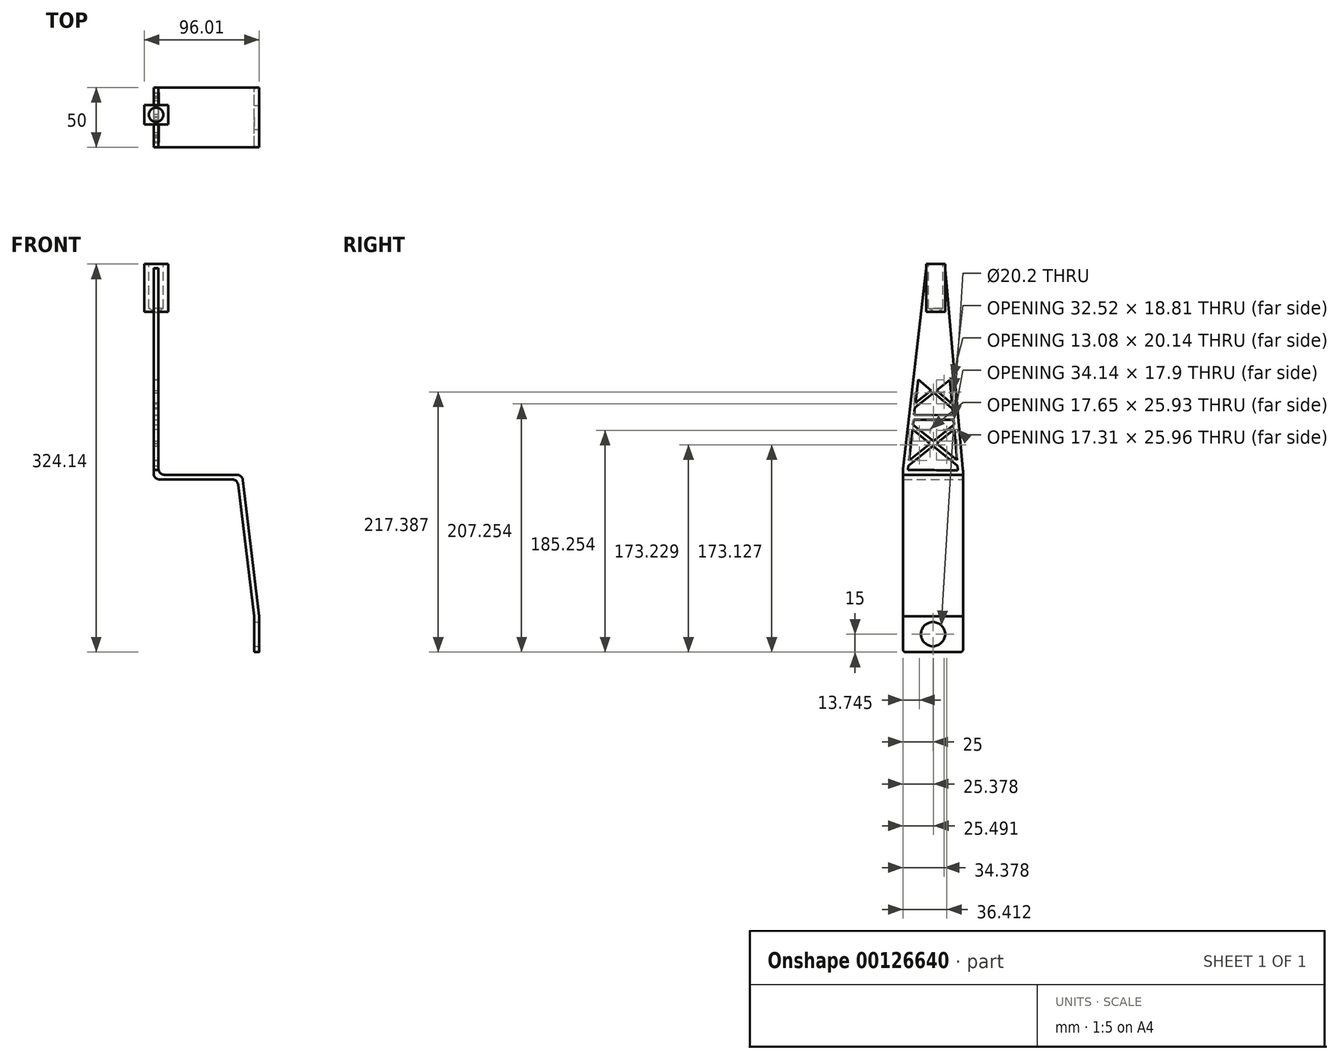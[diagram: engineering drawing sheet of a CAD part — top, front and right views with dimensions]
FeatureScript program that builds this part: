
annotation { "Feature Type Name" : "Feature", "Feature Type Description" : "" }
export const myFeature = defineFeature(function(context is Context, id is Id, definition is map)
    precondition{}
    {
        {
            var Q0;
            Q0=qCreatedBy(makeId("Front.planeOp"),FACE);
            var sketch = newSketch(context, id + "F0", { "sketchPlane" : qUnion([Q0])});
            skLineSegment(sketch, "E0", {"start": v(0, 0) * mm, "end": v(0, 30) * mm});
            skLineSegment(sketch, "E1", {"start": v(0, 30) * mm, "end": v(-14.01, 144.14) * mm});
            skLineSegment(sketch, "E2", {"start": v(0, 30) * mm, "end": v(0, 101.3) * mm, "construction": true});
            skLineSegment(sketch, "E3", {"start": v(-14.01, 144.14) * mm, "end": v(-84.01, 144.14) * mm});
            skLineSegment(sketch, "E4", {"start": v(-84.01, 144.14) * mm, "end": v(-84.01, 324.14) * mm});
            skLineSegment(sketch, "E5", {"start": v(-84.01, 324.14) * mm, "end": v(-80.01, 324.14) * mm});
            skLineSegment(sketch, "E6", {"start": v(-80.01, 324.14) * mm, "end": v(-80.01, 148.14) * mm});
            skLineSegment(sketch, "E7", {"start": v(-80.01, 148.14) * mm, "end": v(-14.01, 148.14) * mm});
            skLineSegment(sketch, "E8", {"start": v(-14.01, 148.14) * mm, "end": v(-10.01, 148.14) * mm});
            skLineSegment(sketch, "E9", {"start": v(4, 30) * mm, "end": v(4, 0) * mm});
            skLineSegment(sketch, "E10", {"start": v(4, 0) * mm, "end": v(0, 0) * mm});
            skLineSegment(sketch, "E11", {"start": v(4, 30) * mm, "end": v(-10.01, 148.14) * mm});
            skSolve(sketch);
        }
        {
            var Q0;
            Q0=qSketchRegion(id+"F0",true);
            extrude(context, id + "F1", {"entities" : qUnion([Q0]), "depth" : 50 * mm});
        }
        {
            var Q0;
            Q0=makeQuery(id+"F1.opExtrude","SWEPT_FACE",FACE,{"disambiguationData":[OSD([sQuery(id+"F0.wireOp",EDGE,"E9")])]});
            var sketch = newSketch(context, id + "F2", { "sketchPlane" : qUnion([Q0])});
            skLineSegment(sketch, "E12.0", {"start": v(0, 30) * mm, "end": v(0, 0) * mm, "construction": true});
            skLineSegment(sketch, "E13", {"start": v(0, 15) * mm, "end": v(-25, 15) * mm, "construction": true});
            skPoint(sketch, "E14", {"position": v(-25, 15) * mm});
            skSolve(sketch);
        }
        {
            var Q0;
            Q0=sQuery(id+"F2.wireOp",VERTEX,"E14");
            var Q1;
            Q1=makeQuery(id+"F1.opExtrude","SWEPT_BODY",BODY,{"disambiguationData":[OSD([sQuery(id+"F0.wireOp",EDGE,"E0"),sQuery(id+"F0.wireOp",EDGE,"E1"),sQuery(id+"F0.wireOp",EDGE,"E3"),sQuery(id+"F0.wireOp",EDGE,"E4"),sQuery(id+"F0.wireOp",EDGE,"E5"),sQuery(id+"F0.wireOp",EDGE,"E6"),sQuery(id+"F0.wireOp",EDGE,"E7"),sQuery(id+"F0.wireOp",EDGE,"E8"),sQuery(id+"F0.wireOp",EDGE,"E9"),sQuery(id+"F0.wireOp",EDGE,"E10"),sQuery(id+"F0.wireOp",EDGE,"E11")])]});
            hole(context, id + "F3", {"style" : HoleStyle.SIMPLE, "endStyle" : HoleEndStyle.THROUGH, "holeDiameter" : 20.2 * mm, "locations" : qUnion([Q0]), "scope" : qUnion([Q1]), "isTappedThrough" : true});
        }
        {
            var Q0;
            Q0=makeQuery(id+"F1.opExtrude","SWEPT_FACE",FACE,{"disambiguationData":[OSD([sQuery(id+"F0.wireOp",EDGE,"E6")])]});
            var sketch = newSketch(context, id + "F4", { "sketchPlane" : qUnion([Q0])});
            skLineSegment(sketch, "E15.0", {"start": v(-50, 324.14) * mm, "end": v(-50, 199.94) * mm, "construction": true});
            skLineSegment(sketch, "E16", {"start": v(-50, 236.14) * mm, "end": v(-50, 324.14) * mm});
            skPoint(sketch, "E17.0.end.orphan", {"position": v(0, 148.14) * mm});
            skLineSegment(sketch, "E18", {"start": v(0, 236.14) * mm, "end": v(0, 199.6) * mm, "construction": true});
            skLineSegment(sketch, "E19", {"start": v(-9.08, 207.31) * mm, "end": v(-37.02, 231.06) * mm});
            skLineSegment(sketch, "E20", {"start": v(-50, 195.94) * mm, "end": v(-50, 199.94) * mm});
            skLineSegment(sketch, "E21", {"start": v(-41.02, 195.94) * mm, "end": v(-8.08, 195.94) * mm});
            skLineSegment(sketch, "E22", {"start": v(-4.52, 155.6) * mm, "end": v(-42.14, 186.09) * mm});
            skLineSegment(sketch, "E23", {"start": v(-50, 194.2) * mm, "end": v(-50, 195.94) * mm});
            skLineSegment(sketch, "E24", {"start": v(-27.43, 174.17) * mm, "end": v(-7.55, 189.95) * mm});
            skLineSegment(sketch, "E25", {"start": v(-50, 156.25) * mm, "end": v(-50, 152.25) * mm});
            skLineSegment(sketch, "E26", {"start": v(-45.58, 155.77) * mm, "end": v(-7.22, 186.2) * mm});
            skLineSegment(sketch, "E27", {"start": v(-50, 152.25) * mm, "end": v(-4.19, 151.81) * mm});
            skLineSegment(sketch, "E28", {"start": v(-30.42, 324.14) * mm, "end": v(0, 324.14) * mm});
            skLineSegment(sketch, "E29", {"start": v(0, 324.14) * mm, "end": v(0, 244.14) * mm});
            skLineSegment(sketch, "E30", {"start": v(-41.22, 194.2) * mm, "end": v(-7.93, 194.2) * mm});
            skLineSegment(sketch, "E31", {"start": v(-50, 152.25) * mm, "end": v(-30.42, 324.14) * mm});
            skLineSegment(sketch, "E32.trimOffspring", {"start": v(-41.7, 190.04) * mm, "end": v(-4.93, 160.25) * mm});
            skLineSegment(sketch, "E33.trimOffspring", {"start": v(-40.77, 198.16) * mm, "end": v(-8.25, 197.85) * mm});
            skLineSegment(sketch, "E34.trimOffspring", {"start": v(-39.6, 208.49) * mm, "end": v(-11.16, 230.87) * mm});
            skLineSegment(sketch, "E35.trimOffspring", {"start": v(-40.1, 204.1) * mm, "end": v(-10.86, 227.46) * mm});
            skLineSegment(sketch, "E36.trimOffspring", {"start": v(-37.4, 227.73) * mm, "end": v(-8.74, 203.37) * mm});
            skLineSegment(sketch, "E37.trimOffspring", {"start": v(-39.99, 240.15) * mm, "end": v(-7.8, 240.28) * mm});
            skLineSegment(sketch, "E38.trimOffspring", {"start": v(-50, 192.46) * mm, "end": v(-50, 148.14) * mm, "construction": true});
            skLineSegment(sketch, "E39.trimOffspring", {"start": v(-50, 195.94) * mm, "end": v(-50, 194.2) * mm, "construction": true});
            skPoint(sketch, "E40.start.orphan", {"position": v(0, 156.25) * mm});
            skLineSegment(sketch, "E41", {"start": v(-27.43, 174.17) * mm, "end": v(-45.08, 160.16) * mm});
            skLineSegment(sketch, "E42", {"start": v(0, 151.81) * mm, "end": v(-15.2, 324.14) * mm});
            skLineSegment(sketch, "E43", {"start": v(-4.19, 151.81) * mm, "end": v(-12, 240.26) * mm});
            skPoint(sketch, "E44.orphan", {"position": v(-35.99, 240.15) * mm});
            skLineSegment(sketch, "E45", {"start": v(-35.99, 240.15) * mm, "end": v(-37.02, 231.06) * mm});
            skLineSegment(sketch, "E46", {"start": v(-37.02, 231.06) * mm, "end": v(-37.4, 227.73) * mm});
            skLineSegment(sketch, "E47", {"start": v(-39.6, 208.49) * mm, "end": v(-37.4, 227.73) * mm});
            skLineSegment(sketch, "E48", {"start": v(-40.1, 204.1) * mm, "end": v(-39.6, 208.49) * mm});
            skLineSegment(sketch, "E49", {"start": v(-40.1, 204.1) * mm, "end": v(-40.77, 198.16) * mm});
            skLineSegment(sketch, "E50", {"start": v(-41.02, 195.94) * mm, "end": v(-40.77, 198.16) * mm});
            skLineSegment(sketch, "E51", {"start": v(-41.22, 194.2) * mm, "end": v(-41.02, 195.94) * mm});
            skLineSegment(sketch, "E52", {"start": v(-41.7, 190.04) * mm, "end": v(-41.22, 194.2) * mm});
            skLineSegment(sketch, "E53", {"start": v(-42.14, 186.09) * mm, "end": v(-41.7, 190.04) * mm});
            skLineSegment(sketch, "E54", {"start": v(-45.08, 160.16) * mm, "end": v(-42.14, 186.09) * mm});
            skLineSegment(sketch, "E55", {"start": v(-45.58, 155.77) * mm, "end": v(-45.08, 160.16) * mm});
            skLineSegment(sketch, "E56", {"start": v(-45.58, 155.77) * mm, "end": v(-45.98, 152.22) * mm});
            skSolve(sketch);
        }
        {
            var Q0;
            {var subQ0=sQuery(id+"F4.wireOp",EDGE,"6JFdQYAn-kcRU-4NtM-X3YT-ezD7Bi678DAS");var subQ3=sQuery(id+"F4.wireOp",EDGE,"GWz0sJcY-8Wv4-S84U-qHgg-poddO3RCVaqC");var subQ4=makeQuery(id+"F4.imprint","INTERSECT",VERTEX,{"derivedFrom":[subQ0,subQ3]});Q0=makeQuery(id+"F4.imprint","IMPRINT",FACE,{"disambiguationData":[TD([[makeQuery(id+"F4.imprint","IMPRINT",EDGE,{"disambiguationData":[TD([[subQ4,1.0]])],"derivedFrom":subQ3}),1.0]])]});}
            var Q1;
            {var subQ0=sQuery(id+"F4.wireOp",EDGE,"PmIU4kkk-4VpV-7eNu-9stD-v7JAOlRvsFyg");Q1=makeQuery(id+"F4.imprint","IMPRINT",FACE,{"disambiguationData":[TD([[makeQuery(id+"F4.imprint","IMPRINT",EDGE,{"derivedFrom":subQ0}),1.0]])]});}
            var Q2;
            {var subQ0=sQuery(id+"F4.wireOp",EDGE,"g6UGt09Z-d0lY-nm8X-FTm8-tr0lM3mQFNzP");Q2=makeQuery(id+"F4.imprint","IMPRINT",FACE,{"disambiguationData":[TD([[makeQuery(id+"F4.imprint","IMPRINT",EDGE,{"derivedFrom":subQ0}),1.0]])]});}
            var Q3;
            {var subQ0=sQuery(id+"F4.wireOp",EDGE,"LF1wSoAy-yxkq-QR4V-37pU-vaxNY6q9ccwR");Q3=makeQuery(id+"F4.imprint","IMPRINT",FACE,{"disambiguationData":[TD([[makeQuery(id+"F4.imprint","IMPRINT",EDGE,{"derivedFrom":subQ0}),1.0]])]});}
            var Q4;
            {var subQ0=sQuery(id+"F4.wireOp",EDGE,"ykEfd208-dPVE-cZZ8-Rbw6-six2oeOVLq18");Q4=makeQuery(id+"F4.imprint","IMPRINT",FACE,{"disambiguationData":[TD([[makeQuery(id+"F4.imprint","IMPRINT",EDGE,{"derivedFrom":subQ0}),1.0]])]});}
            var Q5;
            {var subQ0=sQuery(id+"F4.wireOp",EDGE,"ApeQlJHF-VlI5-qP4p-T5xf-Y3qsMmfdwPXZ");var subQ1=sQuery(id+"F4.wireOp",EDGE,"044ZRw8G-QG9w-9PJM-Aeca-9wbLQxwRHXnp");var subQ2=makeQuery(id+"F4.imprint","INTERSECT",VERTEX,{"derivedFrom":[subQ1,subQ0]});Q5=makeQuery(id+"F4.imprint","IMPRINT",FACE,{"disambiguationData":[TD([[makeQuery(id+"F4.imprint","IMPRINT",EDGE,{"disambiguationData":[TD([[subQ2,-1.0]])],"derivedFrom":subQ1}),-1.0]])]});}
            var Q6;
            {var subQ3=sQuery(id+"F4.wireOp",EDGE,"E19");var subQ5=sQuery(id+"F4.wireOp",EDGE,"sGcRmQGq-mX63-0LLR-Vlmi-zwXAr2PJyINN");var subQ6=makeQuery(id+"F4.imprint","INTERSECT",VERTEX,{"derivedFrom":[subQ3,subQ5]});Q6=makeQuery(id+"F4.imprint","IMPRINT",FACE,{"disambiguationData":[TD([[makeQuery(id+"F4.imprint","IMPRINT",EDGE,{"disambiguationData":[TD([[subQ6,-1.0]])],"derivedFrom":subQ3}),-1.0]])]});}
            var Q7;
            {var subQ0=sQuery(id+"F4.wireOp",EDGE,"WYcAM4oh-6lNs-njuu-vy5P-xPYR0SPUKtF0");var subQ1=sQuery(id+"F4.wireOp",EDGE,"E19");var subQ2=makeQuery(id+"F4.imprint","INTERSECT",VERTEX,{"derivedFrom":[subQ1,subQ0]});Q7=makeQuery(id+"F4.imprint","IMPRINT",FACE,{"disambiguationData":[TD([[makeQuery(id+"F4.imprint","IMPRINT",EDGE,{"disambiguationData":[TD([[subQ2,-1.0]])],"derivedFrom":subQ1}),-1.0]])]});}
            var Q8;
            {var subQ0=sQuery(id+"F4.wireOp",EDGE,"E26");var subQ1=sQuery(id+"F4.wireOp",EDGE,"m9RCNZ96-XPFk-BXaN-ZS9E-6q5Kws0PJv6X");var subQ2=makeQuery(id+"F4.imprint","INTERSECT",VERTEX,{"derivedFrom":[subQ1,subQ0]});Q8=makeQuery(id+"F4.imprint","IMPRINT",FACE,{"disambiguationData":[TD([[makeQuery(id+"F4.imprint","IMPRINT",EDGE,{"disambiguationData":[TD([[subQ2,-1.0]])],"derivedFrom":subQ1}),1.0]])]});}
            var Q9;
            {var subQ0=sQuery(id+"F4.wireOp",EDGE,"E24");var subQ1=sQuery(id+"F4.wireOp",EDGE,"E22");var subQ2=makeQuery(id+"F4.imprint","INTERSECT",VERTEX,{"derivedFrom":[subQ1,subQ0]});Q9=makeQuery(id+"F4.imprint","IMPRINT",FACE,{"disambiguationData":[TD([[makeQuery(id+"F4.imprint","IMPRINT",EDGE,{"disambiguationData":[TD([[subQ2,-1.0]])],"derivedFrom":subQ1}),1.0]])]});}
            var Q10;
            {var subQ5=sQuery(id+"F4.wireOp",EDGE,"CAUZETG8-kMrT-Zt4g-RW8c-leD3wHw1Tw1T");var subQ6=sQuery(id+"F4.wireOp",EDGE,"m9RCNZ96-XPFk-BXaN-ZS9E-6q5Kws0PJv6X");var subQ7=makeQuery(id+"F4.imprint","INTERSECT",VERTEX,{"derivedFrom":[subQ6,subQ5]});Q10=makeQuery(id+"F4.imprint","IMPRINT",FACE,{"disambiguationData":[TD([[makeQuery(id+"F4.imprint","IMPRINT",EDGE,{"disambiguationData":[TD([[subQ7,-1.0]])],"derivedFrom":subQ6}),1.0]])]});}
            var Q11;
            {var subQ1=sQuery(id+"F4.wireOp",EDGE,"044ZRw8G-QG9w-9PJM-Aeca-9wbLQxwRHXnp");var subQ5=sQuery(id+"F4.wireOp",EDGE,"WDKnhBUK-TtAc-dKtc-qf8b-SNADoZVUk4Pq");var subQ6=makeQuery(id+"F4.imprint","INTERSECT",VERTEX,{"derivedFrom":[subQ1,subQ5]});Q11=makeQuery(id+"F4.imprint","IMPRINT",FACE,{"disambiguationData":[TD([[makeQuery(id+"F4.imprint","IMPRINT",EDGE,{"disambiguationData":[TD([[subQ6,-1.0]])],"derivedFrom":subQ1}),-1.0]])]});}
            var Q12;
            {var subQ12=sQuery(id+"F4.wireOp",EDGE,"E16");Q12=makeQuery(id+"F4.imprint","IMPRINT",FACE,{"disambiguationData":[TD([[makeQuery(id+"F4.imprint","IMPRINT",EDGE,{"derivedFrom":subQ12}),1.0]])]});}
            var Q13;
            {var subQ5=sQuery(id+"F4.wireOp",EDGE,"E33.trimOffspring");Q13=makeQuery(id+"F4.imprint","IMPRINT",FACE,{"disambiguationData":[TD([[makeQuery(id+"F4.imprint","IMPRINT",EDGE,{"derivedFrom":subQ5}),1.0]])]});}
            var Q14;
            {var subQ0=sQuery(id+"F4.wireOp",EDGE,"qJwqB984-y6dT-E1cc-qwD0-DkinJdtvzE4B");var subQ1=sQuery(id+"F4.wireOp",EDGE,"E26");var subQ2=makeQuery(id+"F4.imprint","INTERSECT",VERTEX,{"derivedFrom":[subQ1,subQ0]});Q14=makeQuery(id+"F4.imprint","IMPRINT",FACE,{"disambiguationData":[TD([[makeQuery(id+"F4.imprint","IMPRINT",EDGE,{"disambiguationData":[TD([[subQ2,1.0]])],"derivedFrom":subQ1}),-1.0]])]});}
            var Q15;
            {var subQ1=sQuery(id+"F4.wireOp",EDGE,"E30");Q15=makeQuery(id+"F4.imprint","IMPRINT",FACE,{"disambiguationData":[TD([[makeQuery(id+"F4.imprint","IMPRINT",EDGE,{"derivedFrom":subQ1}),-1.0]])]});}
            var Q16;
            {var subQ6=sQuery(id+"F4.wireOp",EDGE,"E29");Q16=makeQuery(id+"F4.imprint","IMPRINT",FACE,{"disambiguationData":[TD([[makeQuery(id+"F4.imprint","IMPRINT",EDGE,{"derivedFrom":subQ6}),-1.0]])]});}
            var Q17;
            {var subQ0=sQuery(id+"F4.wireOp",EDGE,"E43");var subQ7=sQuery(id+"F4.wireOp",EDGE,"E22");var subQ9=makeQuery(id+"F4.imprint","INTERSECT",VERTEX,{"derivedFrom":[subQ7,subQ0]});Q17=makeQuery(id+"F4.imprint","IMPRINT",FACE,{"disambiguationData":[TD([[makeQuery(id+"F4.imprint","IMPRINT",EDGE,{"disambiguationData":[TD([[subQ9,-1.0]])],"derivedFrom":subQ7}),1.0]])]});}
            var Q18;
            {var subQ0=sQuery(id+"F4.wireOp",EDGE,"E47");Q18=makeQuery(id+"F4.imprint","IMPRINT",FACE,{"disambiguationData":[TD([[makeQuery(id+"F4.imprint","IMPRINT",EDGE,{"derivedFrom":subQ0}),-1.0]])]});}
            extrude(context, id + "F5", {"entities" : qUnion([Q0, Q1, Q2, Q3, Q4, Q5, Q6, Q7, Q8, Q9, Q10, Q11, Q12, Q13, Q14, Q15, Q16, Q17, Q18]), "operationType" : NewBodyOperationType.REMOVE, "oppositeDirection" : true, "depth" : 25 * mm});
        }
        {
            var Q0;
            Q0=makeQuery(id+"F1.opExtrude","SWEPT_EDGE",EDGE,{"disambiguationData":[OSD([sQuery(id+"F0.wireOp",EDGE,"E6"),sQuery(id+"F0.wireOp",EDGE,"E7")])]});
            var Q1;
            Q1=makeQuery(id+"F1.opExtrude","SWEPT_EDGE",EDGE,{"disambiguationData":[OSD([sQuery(id+"F0.wireOp",EDGE,"E8"),sQuery(id+"F0.wireOp",EDGE,"E11")])]});
            var Q2;
            Q2=makeQuery(id+"F1.opExtrude","SWEPT_EDGE",EDGE,{"disambiguationData":[OSD([sQuery(id+"F0.wireOp",EDGE,"E3"),sQuery(id+"F0.wireOp",EDGE,"E4")])]});
            var Q3;
            Q3=makeQuery(id+"F1.opExtrude","SWEPT_EDGE",EDGE,{"disambiguationData":[OSD([sQuery(id+"F0.wireOp",EDGE,"E1"),sQuery(id+"F0.wireOp",EDGE,"E3")])]});
            fillet(context, id + "F6", {"entities" : qUnion([Q0, Q1, Q2, Q3]), "radius" : 5 * mm, "tangentPropagation" : true, "allowEdgeOverflow" : false});
        }
        {
            var Q0;
            Q0=makeQuery(id+"F5.boolean.opBoolean","COPY",EDGE,{"derivedFrom":makeQuery(id+"F5.opExtrude","SWEPT_EDGE",EDGE,{"disambiguationData":[OSD([sQuery(id+"F0.wireOp",EDGE,"E6"),sQuery(id+"F4.wireOp",EDGE,"E42")])]})});
            var Q1;
            Q1=makeQuery(id+"F1.opExtrude","CAP_EDGE",EDGE,{"disambiguationData":[OSD([sQuery(id+"F0.wireOp",EDGE,"E10")])],"isStart":false});
            var Q2;
            Q2=makeQuery(id+"F1.opExtrude","CAP_EDGE",EDGE,{"disambiguationData":[OSD([sQuery(id+"F0.wireOp",EDGE,"E10")])],"isStart":true});
            fillet(context, id + "F7", {"entities" : qUnion([Q0, Q1, Q2]), "radius" : 2 * mm, "tangentPropagation" : true, "allowEdgeOverflow" : false});
        }
        {
            var Q0;
            Q0=makeQuery(id+"F1.opExtrude","SWEPT_FACE",FACE,{"disambiguationData":[OSD([sQuery(id+"F0.wireOp",EDGE,"E5")])]});
            var sketch = newSketch(context, id + "F8", { "sketchPlane" : qUnion([Q0])});
            skPoint(sketch, "E57.center.orphan", {"position": v(-80.01, -22.81) * mm});
            skPoint(sketch, "E58", {"position": v(-82.01, -22.81) * mm});
            skPoint(sketch, "E58.positionSnap0", {"position": v(-84.01, -22.81) * mm});
            skPoint(sketch, "E59.top.end.orphan", {"position": v(-90.01, -14.81) * mm});
            skPoint(sketch, "E59.left.end.orphan", {"position": v(-70.01, -14.81) * mm});
            skPoint(sketch, "E59.bottom.end.orphan", {"position": v(-90.01, -30.81) * mm});
            skPoint(sketch, "E59.bottom.start.orphan", {"position": v(-70.01, -30.81) * mm});
            skLineSegment(sketch, "E60.bottom", {"start": v(-72.01, -14.81) * mm, "end": v(-92.01, -14.81) * mm});
            skLineSegment(sketch, "E60.top", {"start": v(-72.01, -30.81) * mm, "end": v(-92.01, -30.81) * mm});
            skLineSegment(sketch, "E60.left", {"start": v(-72.01, -14.81) * mm, "end": v(-72.01, -30.81) * mm});
            skLineSegment(sketch, "E60.right", {"start": v(-92.01, -14.81) * mm, "end": v(-92.01, -30.81) * mm});
            skSolve(sketch);
        }
        {
            var Q0;
            {var subQ0=sQuery(id+"F8.wireOp",EDGE,"E59.bottom");var subQ1=sQuery(id+"F0.wireOp",EDGE,"E5");var subQ2=makeQuery(id+"F1.opExtrude","SWEPT_EDGE",EDGE,{"disambiguationData":[OSD([subQ1,sQuery(id+"F0.wireOp",EDGE,"E6")])]});var subQ3=makeQuery(id+"F8.imprint","INTERSECT",VERTEX,{"derivedFrom":[subQ2,subQ0]});Q0=makeQuery(id+"F8.imprint","IMPRINT",FACE,{"disambiguationData":[TD([[makeQuery(id+"F8.imprint","IMPRINT",EDGE,{"disambiguationData":[TD([[subQ3,-1.0]])],"derivedFrom":subQ0}),-1.0]])]});}
            var Q1;
            Q1=makeQuery(id+"F8.imprint","IMPRINT",FACE,{"disambiguationData":[TD([[makeQuery(id+"F8.imprint","IMPRINT",EDGE,{"derivedFrom":sQuery(id+"F8.wireOp",EDGE,"E60.bottom")}),1.0]])]});
            var Q2;
            {var subQ0=sQuery(id+"F4.wireOp",EDGE,"E28");Q2=makeQuery(id+"F8.imprint","IMPRINT",FACE,{"disambiguationData":[TD([[makeQuery(id+"F8.imprint","IMPRINT",EDGE,{"derivedFrom":makeQuery(id+"F5.boolean.opBoolean","COPY",EDGE,{"derivedFrom":makeQuery(id+"F5.opExtrude","SWEPT_EDGE",EDGE,{"disambiguationData":[OSD([subQ0,sQuery(id+"F4.wireOp",EDGE,"E42")])]})})}),-1.0]])]});}
            extrude(context, id + "F9", {"entities" : qUnion([Q0, Q1, Q2]), "operationType" : NewBodyOperationType.ADD, "oppositeDirection" : true, "depth" : 40 * mm});
        }
        {
            var Q0;
            Q0=sQuery(id+"F8.wireOp",VERTEX,"E58");
            var Q1;
            Q1=makeQuery(id+"F1.opExtrude","SWEPT_BODY",BODY,{"disambiguationData":[OSD([sQuery(id+"F0.wireOp",EDGE,"E0"),sQuery(id+"F0.wireOp",EDGE,"E1"),sQuery(id+"F0.wireOp",EDGE,"E3"),sQuery(id+"F0.wireOp",EDGE,"E4"),sQuery(id+"F0.wireOp",EDGE,"E5"),sQuery(id+"F0.wireOp",EDGE,"E6"),sQuery(id+"F0.wireOp",EDGE,"E7"),sQuery(id+"F0.wireOp",EDGE,"E8"),sQuery(id+"F0.wireOp",EDGE,"E9"),sQuery(id+"F0.wireOp",EDGE,"E10"),sQuery(id+"F0.wireOp",EDGE,"E11")])]});
            hole(context, id + "F10", {"style" : HoleStyle.SIMPLE, "endStyle" : HoleEndStyle.BLIND, "holeDiameter" : 12 * mm, "holeDepth" : 37 * mm, "locations" : qUnion([Q0]), "scope" : qUnion([Q1])});
        }
    });
